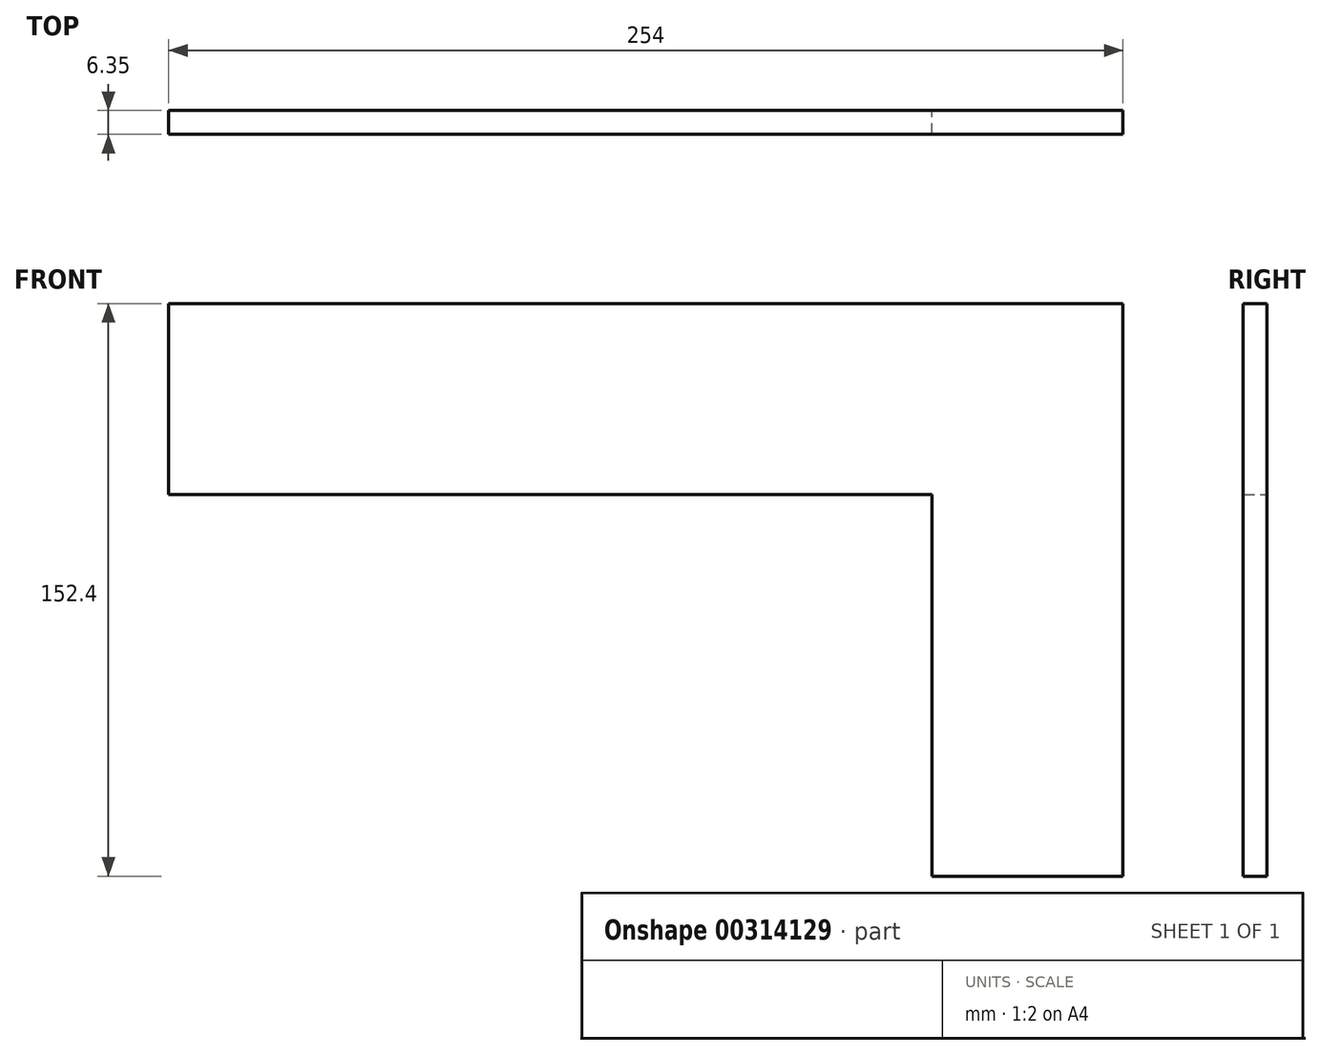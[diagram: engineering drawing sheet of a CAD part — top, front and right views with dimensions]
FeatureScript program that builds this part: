
annotation { "Feature Type Name" : "Feature", "Feature Type Description" : "" }
export const myFeature = defineFeature(function(context is Context, id is Id, definition is map)
    precondition{}
    {
        {
            var Q0;
            Q0=qCreatedBy(makeId("Front.planeOp"),FACE);
            var sketch = newSketch(context, id + "F0", { "sketchPlane" : qUnion([Q0])});
            skLineSegment(sketch, "E0.top", {"start": v(0, 50.8) * mm, "end": v(254, 50.8) * mm});
            skLineSegment(sketch, "E0.left", {"start": v(0, 0) * mm, "end": v(0, 50.8) * mm});
            skLineSegment(sketch, "E0.right", {"start": v(254, 0) * mm, "end": v(254, 50.8) * mm});
            skLineSegment(sketch, "E1", {"start": v(0, 0) * mm, "end": v(203.2, 0) * mm});
            skLineSegment(sketch, "E2", {"start": v(203.2, 0) * mm, "end": v(203.2, -101.6) * mm});
            skLineSegment(sketch, "E3", {"start": v(203.2, -101.6) * mm, "end": v(254, -101.6) * mm});
            skLineSegment(sketch, "E4", {"start": v(254, -101.6) * mm, "end": v(254, 0) * mm});
            skSolve(sketch);
        }
        {
            var Q0;
            Q0=makeQuery(id+"F0.imprint","IMPRINT",FACE,{"disambiguationData":[TD([[makeQuery(id+"F0.imprint","IMPRINT",EDGE,{"derivedFrom":sQuery(id+"F0.wireOp",EDGE,"E0.top")}),-1.0]])]});
            extrude(context, id + "F1", {"entities" : qUnion([Q0]), "depth" : 6.35 * mm});
        }
    });
